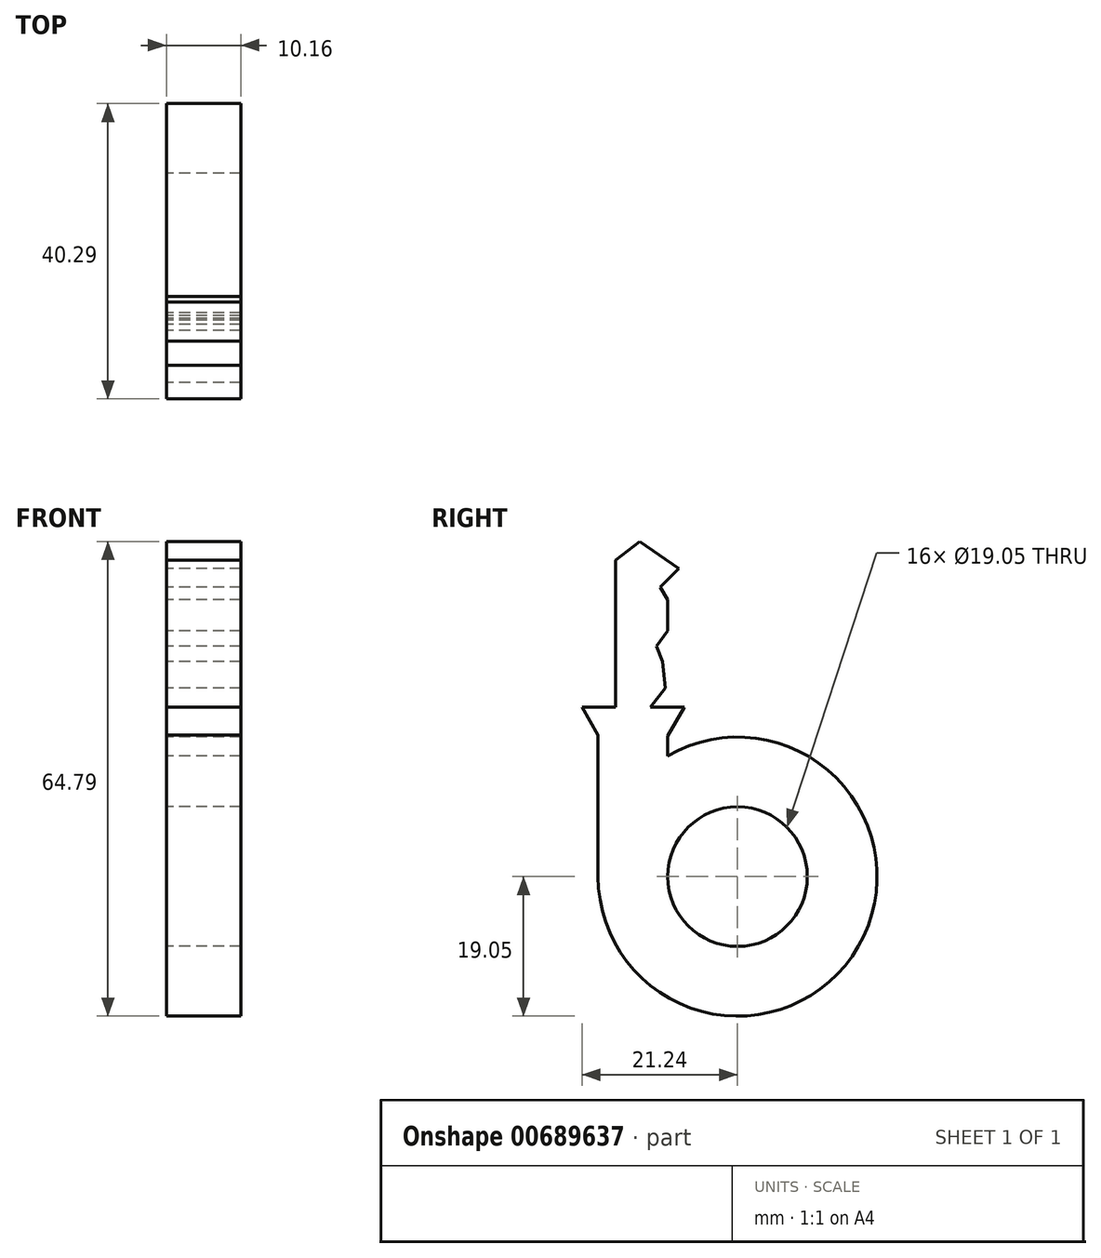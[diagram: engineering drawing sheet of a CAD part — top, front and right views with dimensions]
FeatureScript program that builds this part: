
annotation { "Feature Type Name" : "Feature", "Feature Type Description" : "" }
export const myFeature = defineFeature(function(context is Context, id is Id, definition is map)
    precondition{}
    {
        {
            var Q0;
            Q0=qCreatedBy(makeId("Right.planeOp"),FACE);
            var sketch = newSketch(context, id + "F0", { "sketchPlane" : qUnion([Q0])});
            skCircle(sketch, "E0", {"center": v(0, 0) * mm, "radius": 19.05 * mm});
            skLineSegment(sketch, "E1.bottom", {"start": v(-19.05, 0) * mm, "end": v(-9.52, 0) * mm});
            skLineSegment(sketch, "E1.top", {"start": v(-19.05, 44.45) * mm, "end": v(-9.53, 44.45) * mm});
            skLineSegment(sketch, "E1.left", {"start": v(-19.05, 0) * mm, "end": v(-19.05, 44.45) * mm});
            skLineSegment(sketch, "E1.right", {"start": v(-9.52, 0) * mm, "end": v(-9.53, 44.45) * mm});
            skText(sketch, "E2", { "text": "SIXTH", "fontName": "AllertaStencil-Regular.ttf"});
            skText(sketch, "E3", { "text": "KEY", "fontName": "AllertaStencil-Regular.ttf"});
            skLineSegment(sketch, "E4", {"start": v(-19.05, 19.34) * mm, "end": v(-9.53, 19.2) * mm});
            skLineSegment(sketch, "E5", {"start": v(-19.05, 19.34) * mm, "end": v(-21.24, 23.13) * mm});
            skLineSegment(sketch, "E6", {"start": v(-21.24, 23.13) * mm, "end": v(-7.25, 23.13) * mm});
            skLineSegment(sketch, "E7", {"start": v(-7.25, 23.13) * mm, "end": v(-9.52, 19.2) * mm});
            skPoint(sketch, "E8.middle", {"position": v(-14.17, 33.2) * mm});
            skLineSegment(sketch, "E9", {"start": v(-16.7, 43.2) * mm, "end": v(-13.34, 45.74) * mm});
            skLineSegment(sketch, "E10", {"start": v(-13.34, 45.74) * mm, "end": v(-8.01, 42.06) * mm});
            skLineSegment(sketch, "E11", {"start": v(-8.01, 42.06) * mm, "end": v(-10.54, 39.53) * mm});
            skLineSegment(sketch, "E12", {"start": v(-10.54, 39.53) * mm, "end": v(-9, 36.9) * mm});
            skLineSegment(sketch, "E13", {"start": v(-9, 36.9) * mm, "end": v(-9, 34.27) * mm});
            skLineSegment(sketch, "E14", {"start": v(-9, 34.27) * mm, "end": v(-11.09, 31.47) * mm});
            skLineSegment(sketch, "E15", {"start": v(-11.09, 31.47) * mm, "end": v(-10.23, 29.4) * mm});
            skLineSegment(sketch, "E16", {"start": v(-10.23, 29.4) * mm, "end": v(-9.87, 25.76) * mm});
            skCircle(sketch, "E17", {"center": v(0, 0) * mm, "radius": 9.53 * mm});
            skLineSegment(sketch, "E18.bottom", {"start": v(-16.7, 43.2) * mm, "end": v(-11.93, 43.2) * mm});
            skLineSegment(sketch, "E18.top", {"start": v(-16.7, 23.13) * mm, "end": v(-11.93, 23.13) * mm});
            skLineSegment(sketch, "E18.left", {"start": v(-16.7, 43.2) * mm, "end": v(-16.7, 23.13) * mm});
            skLineSegment(sketch, "E18.right", {"start": v(-11.93, 43.2) * mm, "end": v(-11.93, 23.13) * mm});
            skLineSegment(sketch, "E19", {"start": v(-9.87, 25.76) * mm, "end": v(-11.93, 23.13) * mm});
            const initialGuessF0  = {"E2": [-0.00155, 0.02135, 1, 0, 0.00956], "E3": [0.02044, 0.00826, 1, 0, 0.00952]};
            skSetInitialGuess(sketch, initialGuessF0);
            skSolve(sketch);
        }
        {
            var Q0;
            Q0=makeQuery(id+"F0.imprint","IMPRINT",FACE,{"disambiguationData":[TD([[makeQuery(id+"F0.imprint","IMPRINT",EDGE,{"derivedFrom":sQuery(id+"F0.wireOp",EDGE,"E18.bottom")}),-1.0]])]});
            var Q1;
            {var subQ0=sQuery(id+"F0.wireOp",EDGE,"E15");Q1=makeQuery(id+"F0.imprint","IMPRINT",FACE,{"disambiguationData":[TD([[makeQuery(id+"F0.imprint","IMPRINT",EDGE,{"derivedFrom":subQ0}),-1.0]])]});}
            var Q2;
            {var subQ0=sQuery(id+"F0.wireOp",EDGE,"E11");var subQ1=sQuery(id+"F0.wireOp",EDGE,"E1.right");var subQ2=makeQuery(id+"F0.imprint","INTERSECT",VERTEX,{"derivedFrom":[subQ1,subQ0]});Q2=makeQuery(id+"F0.imprint","IMPRINT",FACE,{"disambiguationData":[TD([[makeQuery(id+"F0.imprint","IMPRINT",EDGE,{"disambiguationData":[TD([[subQ2,-1.0]])],"derivedFrom":subQ1}),-1.0]])]});}
            var Q3;
            {var subQ0=sQuery(id+"F0.wireOp",EDGE,"E9");var subQ1=sQuery(id+"F0.wireOp",EDGE,"E1.top");var subQ2=makeQuery(id+"F0.imprint","INTERSECT",VERTEX,{"derivedFrom":[subQ1,subQ0]});Q3=makeQuery(id+"F0.imprint","IMPRINT",FACE,{"disambiguationData":[TD([[makeQuery(id+"F0.imprint","IMPRINT",EDGE,{"disambiguationData":[TD([[subQ2,-1.0]])],"derivedFrom":subQ1}),1.0]])]});}
            var Q4;
            {var subQ4=sQuery(id+"F0.wireOp",EDGE,"E4");Q4=makeQuery(id+"F0.imprint","IMPRINT",FACE,{"disambiguationData":[TD([[makeQuery(id+"F0.imprint","IMPRINT",EDGE,{"derivedFrom":subQ4}),1.0]])]});}
            var Q5;
            {var subQ0=sQuery(id+"F0.wireOp",EDGE,"E5");Q5=makeQuery(id+"F0.imprint","IMPRINT",FACE,{"disambiguationData":[TD([[makeQuery(id+"F0.imprint","IMPRINT",EDGE,{"derivedFrom":subQ0}),-1.0]])]});}
            var Q6;
            {var subQ0=sQuery(id+"F0.wireOp",EDGE,"E7");Q6=makeQuery(id+"F0.imprint","IMPRINT",FACE,{"disambiguationData":[TD([[makeQuery(id+"F0.imprint","IMPRINT",EDGE,{"derivedFrom":subQ0}),-1.0]])]});}
            var Q7;
            {var subQ5=sQuery(id+"F0.wireOp",EDGE,"E4");Q7=makeQuery(id+"F0.imprint","IMPRINT",FACE,{"disambiguationData":[TD([[makeQuery(id+"F0.imprint","IMPRINT",EDGE,{"derivedFrom":subQ5}),-1.0]])]});}
            var Q8;
            {var subQ0=sQuery(id+"F0.wireOp",EDGE,"E1.bottom");Q8=makeQuery(id+"F0.imprint","IMPRINT",FACE,{"disambiguationData":[TD([[makeQuery(id+"F0.imprint","IMPRINT",EDGE,{"derivedFrom":subQ0}),-1.0]])]});}
            var Q9;
            {var subQ0=sQuery(id+"F0.wireOp",EDGE,"E1.bottom");Q9=makeQuery(id+"F0.imprint","IMPRINT",FACE,{"disambiguationData":[TD([[makeQuery(id+"F0.imprint","IMPRINT",EDGE,{"derivedFrom":subQ0}),1.0]])]});}
            extrude(context, id + "F1", {"entities" : qUnion([Q0, Q1, Q2, Q3, Q4, Q5, Q6, Q7, Q8, Q9]), "depth" : 10.16 * mm, "offsetDistance" : 25.4 * mm});
        }
    });
